FCSTD DOCUMENT  (FreeCAD 0.20R29177 (Git))
Label: Rotor_Magnets
License: All rights reserved
LicenseURL: http://en.wikipedia.org/wiki/All_rights_reserved
objects: App::Link×1, Spreadsheet::Sheet×1, Part::FeaturePython×1
EXTERNAL_REF file=Rotor_Magnet.FCStd obj=Box
EXTERNAL_REF file=../../Master_of_Puppets.FCStd obj=Alternator
EXTERNAL_REF file=../../Master_of_Puppets.FCStd obj=Spreadsheet

FEATURE [App::Link] Link  label="Magnet"
  LinkPlacement = pos=(-25,97.902,0) rot=(0,0,1;0rad)
  LinkedObject = -> <external Rotor_Magnet.FCStd>#Box
  Placement = pos=(-25,97.902,0) rot=(0,0,1;0rad)
  expr: .Placement.Base.x = Spreadsheet.MagnetX
  expr: .Placement.Base.y = Spreadsheet.MagnetY
FEATURE [Spreadsheet::Sheet] Spreadsheet
  cells = A1=Inputs; A2=MagnetWidth; B2(MagnetWidth)==Master_of_Puppets#Spreadsheet.MagnetWidth; A3=MagnetLength; B3(MagnetLength)==Master_of_Puppets#Spreadsheet.MagnetLength; A4=RotorDiskRadius; B4(RotorDiskRadius)==Master_of_Puppets#Spreadsheet.RotorDiskRadius; A5=NumberMagnet; B5(NumberMagnet)==Master_of_Puppets#Spreadsheet.NumberMagnet; A6=DistanceOfMagnetFromCenter; B6(DistanceOfMagnetFromCenter)==Master_of_Puppets#Alternator.DistanceOfMagnetFromCenter; A7=Magnet; A8=MagnetX; B8(MagnetX)==-MagnetWidth / 2; A9=MagnetY; B9(MagnetY)==DistanceOfMagnetFromCenter
FEATURE [Part::FeaturePython] Array  label="Rotor_Magnets"  # Draft array (typed FeaturePython)
  AlwaysSyncPlacement = false
  Angle = 360
  ArrayType = 1
  Axis = (0,0,1)
  Base = -> Link
  Center = (0,0,0)
  Count = 12
  ExpandArray = false
  Fuse = false
  IntervalAxis = (0,0,0)
  IntervalX = (50,0,0)
  IntervalY = (0,50,0)
  IntervalZ = (0,0,50)
  NumberCircles = 3
  NumberPolar = 12
  NumberX = 2
  NumberY = 2
  NumberZ = 1
  Placement = pos=(3.6e-15,0,0) rot=(0,0,1;0rad)
  PlacementList = 12 placements: [(-25,97.902,0),(-70.6016,72.2856,0),(-97.2856,27.3004,0),(-97.902,-25,0),(-72.2856,-70.6016,0),(-27.3004,-97.2856,0),(25,-97.902,0),(70.6016,-72.2856,0),(97.2856,-27.3004,0),(97.902,25,0),(72.2856,70.6016,0),(27.3004,97.2856,0)]
  RadialDistance = 50
  ScaleList = (12) [(1,1,1),(1,1,1),(1,1,1),(1,1,1),(1,1,1),(1,1,1),(1,1,1),(1,1,1),(1,1,1),(1,1,1),(1,1,1),(1,1,1)]
  Symmetry = 1
  TangentialDistance = 25
  expr: NumberPolar = Spreadsheet.NumberMagnet
